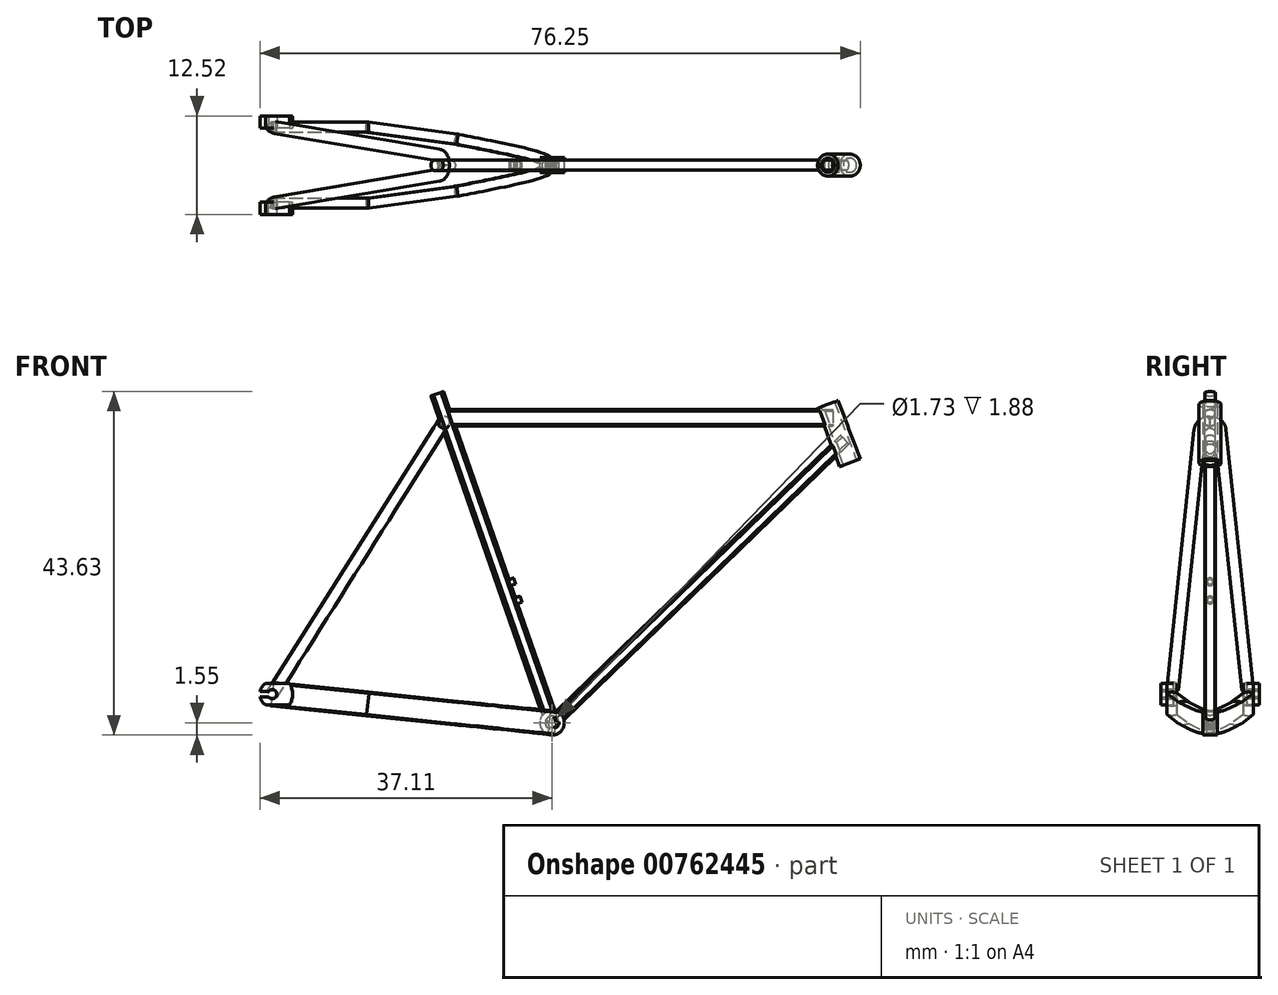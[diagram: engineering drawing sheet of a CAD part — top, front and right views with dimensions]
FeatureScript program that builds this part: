
annotation { "Feature Type Name" : "Feature", "Feature Type Description" : "" }
export const myFeature = defineFeature(function(context is Context, id is Id, definition is map)
    precondition{}
    {
        {
            var Q0;
            Q0=qCreatedBy(makeId("Front.planeOp"),FACE);
            var sketch = newSketch(context, id + "F0", { "sketchPlane" : qUnion([Q0])});
            skLineSegment(sketch, "E0", {"start": v(0, 0) * mm, "end": v(36.83, 35.69) * mm, "construction": true});
            skLineSegment(sketch, "E1", {"start": v(36.83, 35.69) * mm, "end": v(34.5, 41.8) * mm, "construction": true});
            skLineSegment(sketch, "E2", {"start": v(34.5, 41.8) * mm, "end": v(36.83, 35.69) * mm, "construction": true});
            skLineSegment(sketch, "E3", {"start": v(36.83, 35.69) * mm, "end": v(37.83, 33.04) * mm, "construction": true});
            skLineSegment(sketch, "E4", {"start": v(37.83, 33.04) * mm, "end": v(35.67, 38.74) * mm, "construction": true});
            skLineSegment(sketch, "E5", {"start": v(35.67, 38.74) * mm, "end": v(-13.44, 38.74) * mm, "construction": true});
            skLineSegment(sketch, "E6", {"start": v(-13.44, 38.74) * mm, "end": v(-14.6, 41.8) * mm, "construction": true});
            skLineSegment(sketch, "E7", {"start": v(-14.6, 41.8) * mm, "end": v(0, 0) * mm, "construction": true});
            skLineSegment(sketch, "E8", {"start": v(-13.44, 38.74) * mm, "end": v(-35.57, 3.64) * mm, "construction": true});
            skLineSegment(sketch, "E9", {"start": v(-35.57, 3.64) * mm, "end": v(0, 0) * mm, "construction": true});
            skSolve(sketch);
        }
        {
            var Q0;
            Q0=sQuery(id+"F0.wireOp",EDGE,"E0");
            var Q1;
            Q1=sQuery(id+"F0.wireOp",VERTEX,"E7.end");
            cPlane(context, id + "F1", {"entities" : qUnion([Q0, Q1]), "cplaneType" : CPlaneType.LINE_POINT, "offset" : 25.4 * mm, "width" : 152.4 * mm, "height" : 152.4 * mm});
        }
        {
            var Q0;
            Q0=qCreatedBy(id+"F1.planeOp",FACE);
            var sketch = newSketch(context, id + "F2", { "sketchPlane" : qUnion([Q0])});
            skLineSegment(sketch, "E10", {"start": v(0.6, 0.42) * mm, "end": v(0.6, -0.54) * mm});
            skArc(sketch, "E11", {"start": v(0.6, 0.42) * mm, "mid": v(0.34, 0.65) * mm, "end": v(0, 0.73) * mm});
            skArc(sketch, "E12", {"start": v(0.6, -0.54) * mm, "mid": v(0.33, -0.73) * mm, "end": v(0, -0.8) * mm});
            skArc(sketch, "E13.MirrorCS", {"start": v(-0.6, 0.42) * mm, "mid": v(-0.34, 0.65) * mm, "end": v(0, 0.73) * mm});
            skLineSegment(sketch, "E14.MirrorCS", {"start": v(-0.6, 0.42) * mm, "end": v(-0.6, -0.54) * mm});
            skArc(sketch, "E15.MirrorCS", {"start": v(-0.6, -0.54) * mm, "mid": v(-0.33, -0.73) * mm, "end": v(0, -0.8) * mm});
            skSolve(sketch);
        }
        {
            var Q0;
            Q0=makeQuery(id+"F2.imprint","IMPRINT",FACE,{"disambiguationData":[TD([[makeQuery(id+"F2.imprint","IMPRINT",EDGE,{"derivedFrom":sQuery(id+"F2.wireOp",EDGE,"E10")}),-1.0]])]});
            extrude(context, id + "F3", {"entities" : qUnion([Q0]), "depth" : 51.7 * mm, "offsetDistance" : 25.4 * mm});
        }
        {
            var Q0;
            Q0=sQuery(id+"F0.wireOp",EDGE,"E4");
            var Q1;
            Q1=sQuery(id+"F0.wireOp",VERTEX,"E3.end");
            cPlane(context, id + "F4", {"entities" : qUnion([Q0, Q1]), "cplaneType" : CPlaneType.LINE_POINT, "offset" : 25.4 * mm, "width" : 152.4 * mm, "height" : 152.4 * mm});
        }
        {
            var Q0;
            Q0=qCreatedBy(id+"F4.planeOp",FACE);
            var sketch = newSketch(context, id + "F5", { "sketchPlane" : qUnion([Q0])});
            skPoint(sketch, "E16.0", {"position": v(47.1, 0) * mm});
            skCircle(sketch, "E17", {"center": v(47.1, 0) * mm, "radius": 0.9 * mm});
            skCircle(sketch, "E18", {"center": v(47.1, 0) * mm, "radius": 1.4 * mm});
            skSolve(sketch);
        }
        {
            var Q0;
            Q0 = qSketchRegion(id + "F5", true);
            extrude(context, id + "F6", {"entities" : qUnion([Q0]), "operationType" : NewBodyOperationType.ADD, "depth" : 7.92 * mm, "offsetDistance" : 25.4 * mm});
        }
        {
            var Q0;
            Q0=sQuery(id+"F0.wireOp",EDGE,"E5");
            var Q1;
            Q1=sQuery(id+"F0.wireOp",VERTEX,"E5.start");
            cPlane(context, id + "F7", {"entities" : qUnion([Q0, Q1]), "cplaneType" : CPlaneType.LINE_POINT, "offset" : 25.4 * mm, "width" : 152.4 * mm, "height" : 152.4 * mm});
        }
        {
            var Q0;
            Q0=qCreatedBy(id+"F7.planeOp",FACE);
            var sketch = newSketch(context, id + "F8", { "sketchPlane" : qUnion([Q0])});
            skPoint(sketch, "E19.0", {"position": v(0, 38.74) * mm});
            skLineSegment(sketch, "E20.left", {"start": v(-0.63, 39.58) * mm, "end": v(-0.63, 37.9) * mm});
            skLineSegment(sketch, "E20.right", {"start": v(0.63, 39.58) * mm, "end": v(0.63, 37.9) * mm});
            skArc(sketch, "E21", {"start": v(0.63, 39.58) * mm, "mid": v(0, 39.79) * mm, "end": v(-0.63, 39.58) * mm});
            skArc(sketch, "E22", {"start": v(-0.63, 37.9) * mm, "mid": v(0, 37.7) * mm, "end": v(0.63, 37.9) * mm});
            skSolve(sketch);
        }
        {
            var Q0;
            Q0 = qSketchRegion(id + "F8", true);
            extrude(context, id + "F9", {"entities" : qUnion([Q0]), "operationType" : NewBodyOperationType.ADD, "depth" : 50 * mm, "offsetDistance" : 25.4 * mm});
        }
        {
            var Q0;
            Q0=sQuery(id+"F0.wireOp",EDGE,"E7");
            var Q1;
            Q1=sQuery(id+"F0.wireOp",VERTEX,"E7.start");
            cPlane(context, id + "F10", {"entities" : qUnion([Q0, Q1]), "cplaneType" : CPlaneType.LINE_POINT, "offset" : 25.4 * mm, "width" : 152.4 * mm, "height" : 152.4 * mm});
        }
        {
            var Q0;
            Q0=qCreatedBy(id+"F10.planeOp",FACE);
            var sketch = newSketch(context, id + "F11", { "sketchPlane" : qUnion([Q0])});
            skPoint(sketch, "E23.0", {"position": v(0, 0) * mm});
            skLineSegment(sketch, "E24.bottom", {"start": v(0.5, 0.67) * mm, "end": v(-0.5, 0.67) * mm});
            skLineSegment(sketch, "E24.top", {"start": v(0.5, -0.67) * mm, "end": v(-0.5, -0.67) * mm});
            skArc(sketch, "E25", {"start": v(0.5, -0.67) * mm, "mid": v(0.83, 0) * mm, "end": v(0.5, 0.67) * mm});
            skArc(sketch, "E26", {"start": v(-0.5, -0.67) * mm, "mid": v(-0.83, 0) * mm, "end": v(-0.5, 0.67) * mm});
            skSolve(sketch);
        }
        {
            var Q0;
            Q0 = qSketchRegion(id + "F11", true);
            extrude(context, id + "F12", {"entities" : qUnion([Q0]), "operationType" : NewBodyOperationType.ADD, "depth" : 44.8 * mm, "offsetDistance" : 25.4 * mm});
        }
        {
            var Q0;
            Q0=qCreatedBy(makeId("Front.planeOp"),FACE);
            var sketch = newSketch(context, id + "F13", { "sketchPlane" : qUnion([Q0])});
            skCircle(sketch, "E27", {"center": v(0, 0) * mm, "radius": 0.87 * mm});
            skCircle(sketch, "E28", {"center": v(0, 0) * mm, "radius": 1.55 * mm});
            skSolve(sketch);
        }
        {
            var Q0;
            Q0 = qSketchRegion(id + "F13", true);
            extrude(context, id + "F14", {"entities" : qUnion([Q0]), "operationType" : NewBodyOperationType.ADD, "endBound" : BoundingType.SYMMETRIC, "depth" : 1.88 * mm, "offsetDistance" : 25.4 * mm});
        }
        {
            var Q0;
            Q0=sQuery(id+"F0.wireOp",EDGE,"E9");
            cPlane(context, id + "F15", {"entities" : qUnion([Q0]), "cplaneType" : CPlaneType.LINE_ANGLE, "offset" : 25.4 * mm, "angle" : 90 * degree, "width" : 152.4 * mm, "height" : 152.4 * mm});
        }
        {
            var Q0;
            Q0=qCreatedBy(id+"F15.planeOp",FACE);
            var sketch = newSketch(context, id + "F16", { "sketchPlane" : qUnion([Q0])});
            skFitSpline(sketch, "E29", {"points": [v(0, 0) * mm, v(-1.34, 0.84) * mm, v(-7.08, 2.3) * mm, v(-12.24, 3.3) * mm], "startDerivative": vector(-4.9, 4.02) * mm, "endDerivative": vector(-12.62, 2.45) * mm});
            skLineSegment(sketch, "E30", {"start": v(-12.24, 3.3) * mm, "end": v(-23.59, 4.84) * mm});
            skLineSegment(sketch, "E31", {"start": v(-23.59, 4.84) * mm, "end": v(-35.73, 4.84) * mm});
            skSolve(sketch);
        }
        {
            var Q0;
            Q0=sQuery(id+"F16.wireOp",VERTEX,"E31.end");
            var Q1;
            Q1=sQuery(id+"F16.wireOp",EDGE,"E31");
            cPlane(context, id + "F17", {"entities" : qUnion([Q0, Q1]), "cplaneType" : CPlaneType.LINE_POINT, "offset" : 25.4 * mm, "width" : 152.4 * mm, "height" : 152.4 * mm});
        }
        {
            var Q0;
            Q0=qCreatedBy(id+"F17.planeOp",FACE);
            var sketch = newSketch(context, id + "F18", { "sketchPlane" : qUnion([Q0])});
            skPoint(sketch, "E32.0", {"position": v(-4.84, 0) * mm});
            skSolve(sketch);
        }
        {
            var Q0;
            Q0=qCreatedBy(id+"F17.planeOp",FACE);
            var sketch = newSketch(context, id + "F19", { "sketchPlane" : qUnion([Q0])});
            skPoint(sketch, "E33.0", {"position": v(-4.84, 0) * mm});
            skLineSegment(sketch, "E34.left", {"start": v(-4.2, 1.37) * mm, "end": v(-4.2, -1.37) * mm});
            skLineSegment(sketch, "E34.right", {"start": v(-5.47, 1.37) * mm, "end": v(-5.47, -1.37) * mm});
            skArc(sketch, "E35", {"start": v(-5.47, 1.37) * mm, "mid": v(-4.84, 1.5) * mm, "end": v(-4.2, 1.37) * mm});
            skArc(sketch, "E36", {"start": v(-5.47, -1.37) * mm, "mid": v(-4.84, -1.5) * mm, "end": v(-4.2, -1.37) * mm});
            skSolve(sketch);
        }
        {
            var Q0;
            Q0=makeQuery(id+"F19.imprint","IMPRINT",FACE,{"disambiguationData":[TD([[makeQuery(id+"F19.imprint","IMPRINT",EDGE,{"derivedFrom":sQuery(id+"F19.wireOp",EDGE,"E34.left")}),-1.0]])]});
            var Q1;
            Q1=sQuery(id+"F16.wireOp",EDGE,"E31");
            var Q2;
            Q2=sQuery(id+"F16.wireOp",EDGE,"E30");
            var Q3;
            Q3=sQuery(id+"F16.wireOp",EDGE,"E29");
            sweep(context, id + "F20", {"profiles" : qUnion([Q0]), "path" : qUnion([Q1, Q2, Q3])});
        }
        {
            var Q0;
            Q0=makeQuery(id+"F20.opSweep","MID_CAP_EDGE",EDGE,{"disambiguationData":[OSD([sQuery(id+"F16.wireOp",VERTEX,"E29.end"),sQuery(id+"F19.wireOp",EDGE,"E34.right")])],"capPos":2.0});
            var Q1;
            Q1=makeQuery(id+"F20.opSweep","MID_CAP_EDGE",EDGE,{"disambiguationData":[OSD([sQuery(id+"F16.wireOp",VERTEX,"E30.end"),sQuery(id+"F19.wireOp",EDGE,"E34.left")])],"capPos":1.0});
            var Q2;
            Q2=makeQuery(id+"F20.opSweep","MID_CAP_EDGE",EDGE,{"disambiguationData":[OSD([sQuery(id+"F16.wireOp",VERTEX,"E29.end"),sQuery(id+"F19.wireOp",EDGE,"E34.left")])],"capPos":2.0});
            fillet(context, id + "F21", {"entities" : qUnion([Q0, Q1, Q2]), "radius" : 5.08 * mm, "tangentPropagation" : true, "allowEdgeOverflow" : false});
        }
        {
            var Q0;
            Q0=sQuery(id+"F0.wireOp",EDGE,"E8");
            cPlane(context, id + "F22", {"entities" : qUnion([Q0]), "cplaneType" : CPlaneType.LINE_ANGLE, "offset" : 25.4 * mm, "angle" : 0 * degree, "width" : 152.4 * mm, "height" : 152.4 * mm});
        }
        {
            var Q0;
            Q0=qCreatedBy(id+"F22.planeOp",FACE);
            var sketch = newSketch(context, id + "F23", { "sketchPlane" : qUnion([Q0])});
            skPoint(sketch, "E37.0", {"position": v(-4.84, -15.88) * mm});
            skPoint(sketch, "E37.1", {"position": v(0, 24.96) * mm});
            skLineSegment(sketch, "E38", {"start": v(-4.84, -15.88) * mm, "end": v(-1.29, 23.77) * mm});
            skArc(sketch, "E39", {"start": v(0, 24.96) * mm, "mid": v(-0.87, 24.61) * mm, "end": v(-1.29, 23.77) * mm});
            skSolve(sketch);
        }
        {
            var Q0;
            Q0=sQuery(id+"F23.wireOp",EDGE,"E38");
            var Q1;
            Q1=sQuery(id+"F19.wireOp",VERTEX,"E33.0");
            cPlane(context, id + "F24", {"entities" : qUnion([Q0, Q1]), "cplaneType" : CPlaneType.LINE_POINT, "offset" : 25.4 * mm, "width" : 152.4 * mm, "height" : 152.4 * mm});
        }
        {
            var Q0;
            Q0=qCreatedBy(id+"F24.planeOp",FACE);
            var sketch = newSketch(context, id + "F25", { "sketchPlane" : qUnion([Q0])});
            skPoint(sketch, "E40.0", {"position": v(-31.77, 5.2) * mm});
            skCircle(sketch, "E41", {"center": v(-31.77, 5.2) * mm, "radius": 0.75 * mm});
            skSolve(sketch);
        }
        {
            var Q0;
            Q0=makeQuery(id+"F25.imprint","IMPRINT",FACE,{"disambiguationData":[TD([[makeQuery(id+"F25.imprint","IMPRINT",EDGE,{"derivedFrom":sQuery(id+"F25.wireOp",EDGE,"E41")}),1.0]])]});
            var Q1;
            Q1=sQuery(id+"F23.wireOp",EDGE,"E38");
            var Q2;
            Q2=sQuery(id+"F23.wireOp",EDGE,"E39");
            sweep(context, id + "F26", {"profiles" : qUnion([Q0]), "path" : qUnion([Q1, Q2])});
        }
        {
            var Q0;
            Q0=makeQuery(id+"F20.opSweep","SWEPT_FACE",FACE,{"disambiguationData":[OSD([sQuery(id+"F16.wireOp",EDGE,"E31"),sQuery(id+"F19.wireOp",EDGE,"E34.right")])]});
            var sketch = newSketch(context, id + "F27", { "sketchPlane" : qUnion([Q0])});
            skLineSegment(sketch, "E42.bottom", {"start": v(33.35, 2.28) * mm, "end": v(36.38, 2.28) * mm});
            skLineSegment(sketch, "E42.top", {"start": v(33.35, 5) * mm, "end": v(36.38, 5) * mm});
            skPoint(sketch, "E42.middle", {"position": v(35.55, 3.64) * mm});
            skArc(sketch, "E43", {"start": v(33.35, 5) * mm, "mid": v(32.97, 3.64) * mm, "end": v(33.35, 2.28) * mm});
            skArc(sketch, "E44", {"start": v(36.38, 5) * mm, "mid": v(36.85, 4.57) * mm, "end": v(37.1, 4) * mm});
            skLineSegment(sketch, "E45", {"start": v(35.55, 3.64) * mm, "end": v(37.74, 3.64) * mm, "construction": true});
            skArc(sketch, "E46.MirrorCS", {"start": v(36.38, 2.28) * mm, "mid": v(36.85, 2.71) * mm, "end": v(37.1, 3.3) * mm});
            skLineSegment(sketch, "E47", {"start": v(37.1, 3.3) * mm, "end": v(36.01, 3.3) * mm});
            skArc(sketch, "E48", {"start": v(36.01, 4) * mm, "mid": v(34.96, 3.64) * mm, "end": v(36.01, 3.3) * mm});
            skLineSegment(sketch, "E49.MirrorCS", {"start": v(37.1, 4) * mm, "end": v(36.01, 4) * mm});
            skPoint(sketch, "E50.orphan", {"position": v(37.74, 2.28) * mm});
            skPoint(sketch, "E51.orphan", {"position": v(37.74, 5) * mm});
            skSolve(sketch);
        }
        {
            var Q0;
            Q0 = qSketchRegion(id + "F27", true);
            extrude(context, id + "F28", {"entities" : qUnion([Q0]), "endBound" : BoundingType.SYMMETRIC, "depth" : 1.57 * mm, "offsetDistance" : 25.4 * mm});
        }
        {
            var Q0;
            Q0=makeQuery(id+"F28.opExtrude","CAP_FACE",FACE,{"disambiguationData":[OSD([sQuery(id+"F27.wireOp",EDGE,"E42.bottom"),sQuery(id+"F27.wireOp",EDGE,"E42.top"),sQuery(id+"F27.wireOp",EDGE,"E43"),sQuery(id+"F27.wireOp",EDGE,"E44"),sQuery(id+"F27.wireOp",EDGE,"E46.MirrorCS"),sQuery(id+"F27.wireOp",EDGE,"E47"),sQuery(id+"F27.wireOp",EDGE,"E48"),sQuery(id+"F27.wireOp",EDGE,"E49.MirrorCS")])],"isStart":false});
            var sketch = newSketch(context, id + "F29", { "sketchPlane" : qUnion([Q0])});
            skCircle(sketch, "E52", {"center": v(35.55, 3.64) * mm, "radius": 0.57 * mm});
            skSolve(sketch);
        }
        {
            var Q0;
            Q0 = qSketchRegion(id + "F29", true);
            extrude(context, id + "F30", {"entities" : qUnion([Q0]), "operationType" : NewBodyOperationType.REMOVE, "oppositeDirection" : true, "depth" : 25.4 * mm, "offsetDistance" : 25.4 * mm});
        }
        {
            var Q0;
            Q0=makeQuery(id+"F20.opSweep","SWEPT_BODY",BODY,{"disambiguationData":[OSD([sQuery(id+"F16.wireOp",EDGE,"E29"),sQuery(id+"F19.wireOp",EDGE,"E34.left"),sQuery(id+"F19.wireOp",EDGE,"E34.right"),sQuery(id+"F19.wireOp",EDGE,"E35"),sQuery(id+"F19.wireOp",EDGE,"E36")])]});
            var Q1;
            Q1=makeQuery(id+"F26.opSweep","SWEPT_BODY",BODY,{"disambiguationData":[OSD([sQuery(id+"F23.wireOp",EDGE,"E39"),sQuery(id+"F25.wireOp",EDGE,"E41")])]});
            var Q2;
            Q2=makeQuery(id+"F28.opExtrude","SWEPT_BODY",BODY,{"disambiguationData":[OSD([sQuery(id+"F27.wireOp",EDGE,"E42.bottom"),sQuery(id+"F27.wireOp",EDGE,"E42.top"),sQuery(id+"F27.wireOp",EDGE,"E43"),sQuery(id+"F27.wireOp",EDGE,"E44"),sQuery(id+"F27.wireOp",EDGE,"E46.MirrorCS"),sQuery(id+"F27.wireOp",EDGE,"E47"),sQuery(id+"F27.wireOp",EDGE,"E48"),sQuery(id+"F27.wireOp",EDGE,"E49.MirrorCS")])]});
            var Q3;
            Q3=qCreatedBy(makeId("Front.planeOp"),FACE);
            mirror(context, id + "F31", {"entities" : qUnion([Q0, Q1, Q2]), "mirrorPlane" : qUnion([Q3])});
        }
        {
            var Q0;
            {var subQ1=sQuery(id+"F11.wireOp",EDGE,"E25");Q0=makeQuery(id+"F14.boolean.opBoolean","SPLIT",FACE,{"disambiguationData":[TD([makeQuery(id+"F9.opExtrude","SWEPT_FACE",FACE,{"disambiguationData":[OSD([sQuery(id+"F8.wireOp",EDGE,"E20.left")])]})])],"derivedFrom":makeQuery(id+"F12.opExtrude","SWEPT_FACE",FACE,{"disambiguationData":[OSD([subQ1])]})});}
            cPlane(context, id + "F32", {"entities" : qUnion([Q0]), "cplaneType" : CPlaneType.LINE_ANGLE, "offset" : 25.4 * mm, "angle" : 0 * degree, "width" : 152.4 * mm, "height" : 152.4 * mm});
        }
        {
            var Q0;
            Q0=qCreatedBy(id+"F32.planeOp",FACE);
            var sketch = newSketch(context, id + "F33", { "sketchPlane" : qUnion([Q0])});
            skLineSegment(sketch, "E53.0", {"start": v(0, 44.28) * mm, "end": v(0, 0) * mm});
            skCircle(sketch, "E54", {"center": v(0, 18.58) * mm, "radius": 0.4 * mm});
            skCircle(sketch, "E55", {"center": v(0, 16.13) * mm, "radius": 0.4 * mm});
            skSolve(sketch);
        }
        {
            var Q0;
            Q0 = qSketchRegion(id + "F33", true);
            extrude(context, id + "F34", {"entities" : qUnion([Q0]), "operationType" : NewBodyOperationType.ADD, "depth" : 1.45 * mm, "offsetDistance" : 25.4 * mm});
        }
        {
            var Q0;
            Q0=sQuery(id+"F0.wireOp",EDGE,"E2");
            cPoint(context, id + "F35", {"entities" : qUnion([Q0]), "parameter" : 0.5});
        }
        {
            var Q0;
            Q0=sQuery(id+"F0.wireOp",VERTEX,"E9.start");
            var Q1;
            Q1=sQuery(id+"F11.wireOp",VERTEX,"E23.0");
            var Q2;
            Q2 = qCreatedBy(id + "F35" ,VERTEX);
            cPlane(context, id + "F36", {"entities" : qUnion([Q0, Q1, Q2]), "cplaneType" : CPlaneType.THREE_POINT, "offset" : 25.4 * mm, "width" : 152.4 * mm, "height" : 152.4 * mm});
        }
    });
